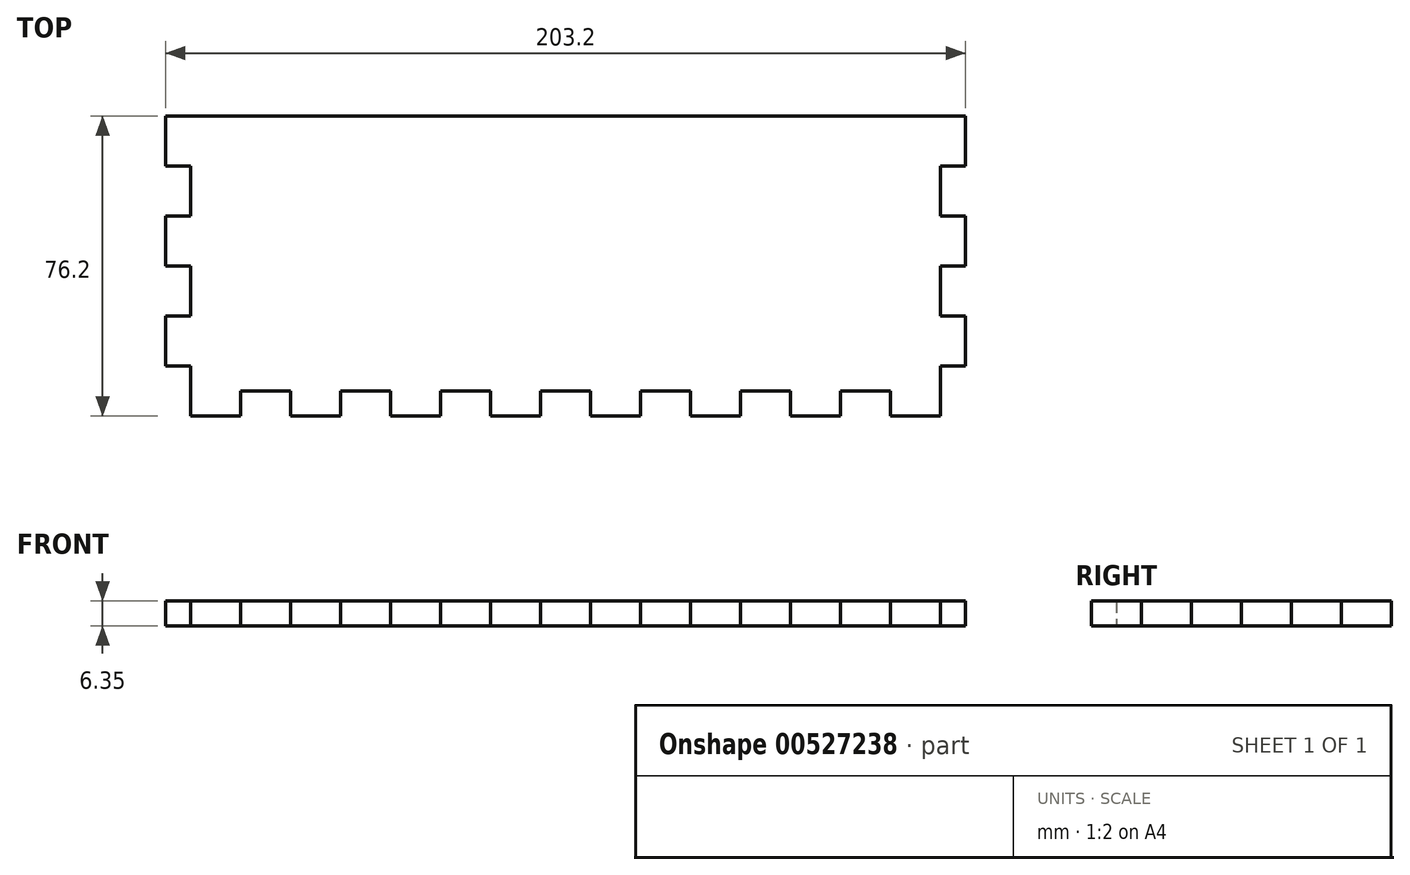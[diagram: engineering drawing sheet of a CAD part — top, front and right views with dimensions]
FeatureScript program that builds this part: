
annotation { "Feature Type Name" : "Feature", "Feature Type Description" : "" }
export const myFeature = defineFeature(function(context is Context, id is Id, definition is map)
    precondition{}
    {
        {
            var Q0;
            Q0=qCreatedBy(makeId("Top.planeOp"),FACE);
            var sketch = newSketch(context, id + "F0", { "sketchPlane" : qUnion([Q0])});
            skLineSegment(sketch, "E0.bottom", {"start": v(0, 0) * mm, "end": v(203.2, 0) * mm});
            skLineSegment(sketch, "E0.left", {"start": v(0, 0) * mm, "end": v(0, -12.7) * mm});
            skLineSegment(sketch, "E1", {"start": v(6.35, -76.2) * mm, "end": v(6.35, -63.5) * mm});
            skLineSegment(sketch, "E2", {"start": v(6.35, -63.5) * mm, "end": v(0, -63.5) * mm});
            skLineSegment(sketch, "E3", {"start": v(0, -63.5) * mm, "end": v(0, -50.8) * mm});
            skLineSegment(sketch, "E4", {"start": v(0, -50.8) * mm, "end": v(6.35, -50.8) * mm});
            skLineSegment(sketch, "E5", {"start": v(6.35, -50.8) * mm, "end": v(6.35, -38.1) * mm});
            skLineSegment(sketch, "E6", {"start": v(6.35, -38.1) * mm, "end": v(0, -38.1) * mm});
            skLineSegment(sketch, "E7", {"start": v(0, -38.1) * mm, "end": v(0, -25.4) * mm});
            skLineSegment(sketch, "E8", {"start": v(0, -25.4) * mm, "end": v(6.35, -25.4) * mm});
            skLineSegment(sketch, "E9", {"start": v(6.35, -25.4) * mm, "end": v(6.35, -12.7) * mm});
            skLineSegment(sketch, "E10", {"start": v(6.35, -12.7) * mm, "end": v(0, -12.7) * mm});
            skLineSegment(sketch, "E11.trimOffspring", {"start": v(0, -25.4) * mm, "end": v(0, -38.1) * mm});
            skLineSegment(sketch, "E12.trimOffspring", {"start": v(0, -50.8) * mm, "end": v(0, -63.5) * mm});
            skPoint(sketch, "E13.orphan", {"position": v(0, -76.2) * mm});
            skLineSegment(sketch, "E14", {"start": v(19.05, -69.85) * mm, "end": v(31.75, -69.85) * mm});
            skLineSegment(sketch, "E15", {"start": v(31.75, -69.85) * mm, "end": v(31.75, -76.2) * mm});
            skLineSegment(sketch, "E16", {"start": v(31.75, -76.2) * mm, "end": v(44.45, -76.2) * mm});
            skLineSegment(sketch, "E17", {"start": v(44.45, -76.2) * mm, "end": v(44.45, -69.85) * mm});
            skLineSegment(sketch, "E18", {"start": v(44.45, -69.85) * mm, "end": v(57.15, -69.85) * mm});
            skLineSegment(sketch, "E19", {"start": v(57.15, -69.85) * mm, "end": v(57.15, -76.2) * mm});
            skLineSegment(sketch, "E20", {"start": v(57.15, -76.2) * mm, "end": v(69.85, -76.2) * mm});
            skLineSegment(sketch, "E21", {"start": v(69.85, -76.2) * mm, "end": v(69.85, -69.85) * mm});
            skLineSegment(sketch, "E22", {"start": v(69.85, -69.85) * mm, "end": v(82.55, -69.85) * mm});
            skLineSegment(sketch, "E23", {"start": v(82.55, -69.85) * mm, "end": v(82.55, -76.2) * mm});
            skLineSegment(sketch, "E24", {"start": v(82.55, -76.2) * mm, "end": v(95.25, -76.2) * mm});
            skLineSegment(sketch, "E25", {"start": v(95.25, -76.2) * mm, "end": v(95.25, -69.85) * mm});
            skLineSegment(sketch, "E26", {"start": v(95.25, -69.85) * mm, "end": v(107.95, -69.85) * mm});
            skLineSegment(sketch, "E27", {"start": v(107.95, -69.85) * mm, "end": v(107.95, -76.2) * mm});
            skLineSegment(sketch, "E28", {"start": v(107.95, -76.2) * mm, "end": v(120.65, -76.2) * mm});
            skLineSegment(sketch, "E29", {"start": v(120.65, -76.2) * mm, "end": v(120.65, -69.85) * mm});
            skLineSegment(sketch, "E30", {"start": v(120.65, -69.85) * mm, "end": v(133.35, -69.85) * mm});
            skLineSegment(sketch, "E31", {"start": v(133.35, -69.85) * mm, "end": v(133.35, -76.2) * mm});
            skLineSegment(sketch, "E32", {"start": v(133.35, -76.2) * mm, "end": v(146.05, -76.2) * mm});
            skLineSegment(sketch, "E33", {"start": v(146.05, -76.2) * mm, "end": v(146.05, -69.85) * mm});
            skLineSegment(sketch, "E34", {"start": v(146.05, -69.85) * mm, "end": v(158.75, -69.85) * mm});
            skLineSegment(sketch, "E35", {"start": v(158.75, -69.85) * mm, "end": v(158.75, -76.2) * mm});
            skLineSegment(sketch, "E36", {"start": v(158.75, -76.2) * mm, "end": v(171.45, -76.2) * mm});
            skLineSegment(sketch, "E37", {"start": v(171.45, -76.2) * mm, "end": v(171.45, -69.85) * mm});
            skLineSegment(sketch, "E38", {"start": v(171.45, -69.85) * mm, "end": v(184.15, -69.85) * mm});
            skLineSegment(sketch, "E39", {"start": v(196.85, -76.2) * mm, "end": v(196.85, -63.5) * mm});
            skLineSegment(sketch, "E40", {"start": v(196.85, -63.5) * mm, "end": v(203.2, -63.5) * mm});
            skLineSegment(sketch, "E41", {"start": v(101.6, -69.85) * mm, "end": v(101.6, -42.53) * mm, "construction": true});
            skLineSegment(sketch, "E42.MirrorCS", {"start": v(203.2, -63.5) * mm, "end": v(203.2, -50.8) * mm});
            skLineSegment(sketch, "E43.MirrorCS", {"start": v(203.2, -50.8) * mm, "end": v(196.85, -50.8) * mm});
            skLineSegment(sketch, "E44.MirrorCS", {"start": v(196.85, -50.8) * mm, "end": v(196.85, -38.1) * mm});
            skLineSegment(sketch, "E45.MirrorCS", {"start": v(196.85, -38.1) * mm, "end": v(203.2, -38.1) * mm});
            skLineSegment(sketch, "E46.MirrorCS", {"start": v(203.2, -38.1) * mm, "end": v(203.2, -25.4) * mm});
            skLineSegment(sketch, "E47.MirrorCS", {"start": v(203.2, -25.4) * mm, "end": v(196.85, -25.4) * mm});
            skLineSegment(sketch, "E48.MirrorCS", {"start": v(196.85, -25.4) * mm, "end": v(196.85, -12.7) * mm});
            skLineSegment(sketch, "E49.MirrorCS", {"start": v(196.85, -12.7) * mm, "end": v(203.2, -12.7) * mm});
            skLineSegment(sketch, "E50.MirrorCS", {"start": v(203.2, 0) * mm, "end": v(203.2, -12.7) * mm});
            skLineSegment(sketch, "E51", {"start": v(19.05, -69.85) * mm, "end": v(19.05, -76.2) * mm});
            skLineSegment(sketch, "E52", {"start": v(6.35, -76.2) * mm, "end": v(19.05, -76.2) * mm});
            skLineSegment(sketch, "E53", {"start": v(184.15, -76.2) * mm, "end": v(184.15, -69.85) * mm});
            skLineSegment(sketch, "E54", {"start": v(184.15, -76.2) * mm, "end": v(196.85, -76.2) * mm});
            skSolve(sketch);
        }
        {
            var Q0;
            Q0=makeQuery(id+"F0.imprint","IMPRINT",FACE,{"disambiguationData":[TD([[makeQuery(id+"F0.imprint","IMPRINT",EDGE,{"derivedFrom":sQuery(id+"F0.wireOp",EDGE,"E0.bottom")}),-1.0]])]});
            extrude(context, id + "F1", {"entities" : qUnion([Q0]), "depth" : 6.35 * mm, "offsetDistance" : 25.4 * mm});
        }
    });
